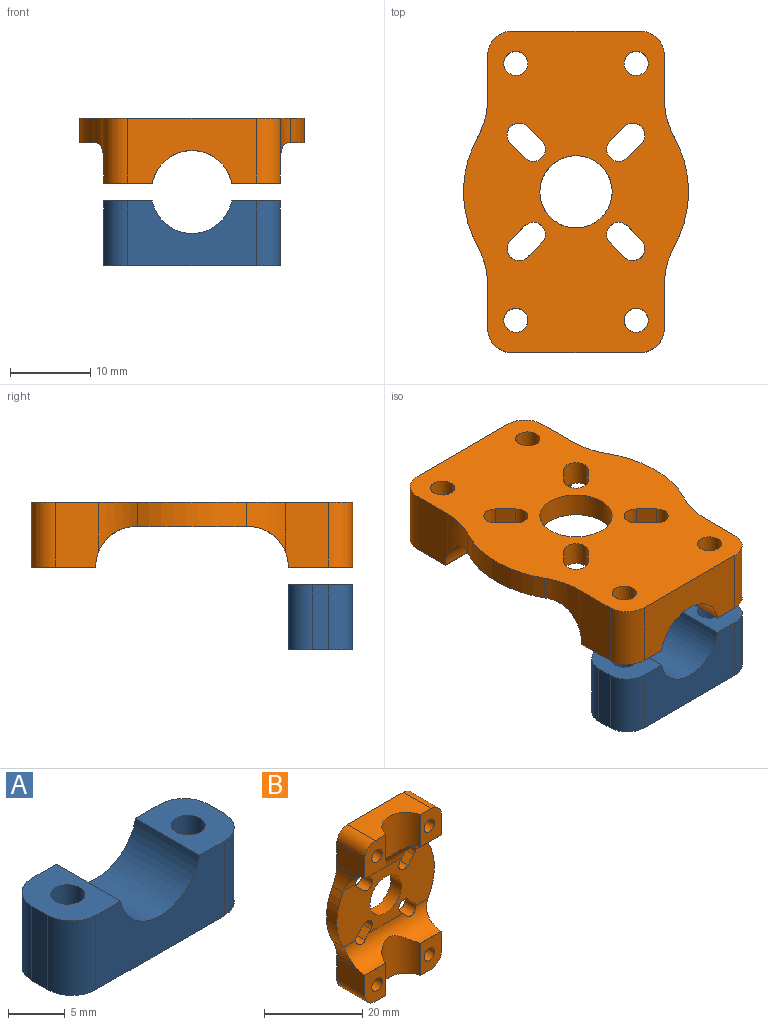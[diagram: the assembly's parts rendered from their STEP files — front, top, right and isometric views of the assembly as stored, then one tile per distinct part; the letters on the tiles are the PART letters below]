
ASSEMBLY  parts=2 mates=2
PART A: 14 faces, bbox 22x8x8.1 mm
  f0: cylinder r=5.05mm len=9.9mm, axis (0,1,0), area 110.8mm2, adj f3,f4,f5,f9
  f1: plane 22x8mm, normal (0,0,-1), area 154.1mm2, adj f2,f4,f5,f6,f7,f8,f10,f11
  f2: plane 8.05x2mm, normal (1,0,0), area 16.1mm2, adj f1,f3,f7,f8
  f3: plane 8x6.05mm, normal (0,0,1), area 37.5mm2, adj f0,f2,f4,f5,f6,f7,f8
  f4: plane 16x8.05mm, normal (0,-1,0), area 98.8mm2, adj f0,f1,f3,f8,f9,f13
  f5: plane 16x8.05mm, normal (0,1,0), area 98.8mm2, adj f0,f1,f3,f7,f9,f12
  f6: cylinder r=1.5mm len=8.05mm, axis (0,0,1), area 75.9mm2, adj f1,f3
  f7: cylinder r=3mm len=8.05mm, axis (0,0,1), area 37.9mm2, adj f1,f2,f3,f5
  f8: cylinder r=3mm len=8.05mm, axis (0,0,-1), area 37.9mm2, adj f1,f2,f3,f4
  f9: plane 8x6.05mm, normal (0,0,1), area 37.5mm2, adj f0,f4,f5,f10,f11,f12,f13
  f10: plane 8.05x2mm, normal (-1,0,0), area 16.1mm2, adj f1,f9,f12,f13
  f11: cylinder r=1.5mm len=8.05mm, axis (0,0,1), area 75.9mm2, adj f1,f9
  f12: cylinder r=3mm len=8.05mm, axis (0,0,-1), area 37.9mm2, adj f1,f5,f9,f10
  f13: cylinder r=3mm len=8.05mm, axis (0,0,1), area 37.9mm2, adj f1,f4,f9,f10
PART B: 51 faces, bbox 28x8.1x40 mm
  f0: plane 6.06x0.05mm, normal (0,0,-1), area 0.3mm2, adj f27,f28,f36,f46
  f1: plane 6.06x0.05mm, normal (0,0,1), area 0.3mm2, adj f29,f30,f31,f45
  f2: plane 16x8.05mm, normal (0,0,1), area 98.8mm2, adj f4,f5,f27,f28,f41,f42
  f3: plane 28x14mm, normal (0,-1,0), area 269.2mm2, adj f10,f11,f12,f13,f14,f15,f16,f17
  f4: plane 40x28mm, normal (0,1,0), area 795.9mm2, adj f2,f9,f10,f11,f12,f13,f14,f15
  f5: plane 8x6.05mm, normal (0,-1,0), area 39.4mm2, adj f2,f6,f28,f35,f39,f42
  f6: plane 6.06x0.05mm, normal (0,0,-1), area 0.3mm2, adj f5,f28,f35,f46
  f7: plane 8x6.05mm, normal (0,-1,0), area 39.4mm2, adj f8,f9,f30,f34,f38,f43
  f8: plane 6.06x0.05mm, normal (0,0,1), area 0.3mm2, adj f7,f30,f34,f45
  f9: plane 16x8.05mm, normal (0,0,-1), area 98.8mm2, adj f4,f7,f29,f30,f43,f44
  f10: cylinder r=1.5mm len=3mm, axis (0,-1,0), area 14.1mm2, adj f3,f4,f11,f25
  f11: plane 3x1.77mm, normal (0.71,0,0.71), area 7.5mm2, adj f3,f4,f10,f12
  f12: cylinder r=1.5mm len=3.25mm, axis (0,-1,0), area 14.7mm2, adj f3,f4,f11,f25,f46
  f13: plane 3x1.77mm, normal (0.71,0,-0.71), area 7.5mm2, adj f3,f4,f14,f22
  f14: cylinder r=1.5mm len=3mm, axis (0,-1,0), area 14.1mm2, adj f3,f4,f13,f15
  f15: plane 3.14x1.78mm, normal (-0.71,0,0.71), area 7.6mm2, adj f3,f4,f14,f22,f45
  f16: plane 3.14x1.78mm, normal (0.71,0,0.71), area 7.6mm2, adj f3,f4,f17,f23,f45
  f17: cylinder r=1.5mm len=3mm, axis (0,-1,0), area 14.1mm2, adj f3,f4,f16,f18
  f18: plane 3x1.77mm, normal (-0.71,0,-0.71), area 7.5mm2, adj f3,f4,f17,f23
  f19: plane 3x1.77mm, normal (-0.71,0,0.71), area 7.5mm2, adj f3,f4,f20,f24
  f20: cylinder r=1.5mm len=3mm, axis (0,-1,0), area 14.1mm2, adj f3,f4,f19,f21
  f21: plane 3.14x1.78mm, normal (0.71,0,-0.71), area 7.6mm2, adj f3,f4,f20,f24,f46
  f22: cylinder r=1.5mm len=3.25mm, axis (0,-1,0), area 14.7mm2, adj f3,f4,f13,f15,f45
  f23: cylinder r=1.5mm len=3.25mm, axis (0,-1,0), area 14.7mm2, adj f3,f4,f16,f18,f45
  f24: cylinder r=1.5mm len=3.25mm, axis (0,-1,0), area 14.7mm2, adj f3,f4,f19,f21,f46
  f25: plane 3.14x1.78mm, normal (-0.71,0,-0.71), area 7.6mm2, adj f3,f4,f10,f12,f46
  f26: cylinder r=4.5mm len=9mm, axis (0,1,0), area 84.8mm2, adj f3,f4
  f27: plane 8x6.05mm, normal (0,-1,0), area 39.4mm2, adj f0,f2,f28,f36,f40,f41
  f28: cylinder r=5.05mm len=10mm, axis (0,0,1), area 123.9mm2, adj f0,f2,f5,f6,f27,f46
  f29: plane 8x6.05mm, normal (0,-1,0), area 39.4mm2, adj f1,f9,f30,f31,f37,f44
  f30: cylinder r=5.05mm len=10mm, axis (0,0,-1), area 123.9mm2, adj f1,f7,f8,f9,f29,f45
  f31: plane 8.05x5.38mm, normal (1,0,0), area 42.8mm2, adj f1,f4,f29,f44,f45,f50
  f32: cylinder r=14mm len=13.56mm, axis (0,1,0), area 42.5mm2, adj f3,f4,f48,f50
  f33: cylinder r=14mm len=13.56mm, axis (0,1,0), area 42.5mm2, adj f3,f4,f47,f49
  f34: plane 8.05x5.38mm, normal (-1,0,0), area 42.8mm2, adj f4,f7,f8,f43,f45,f49
  f35: plane 8.05x5.38mm, normal (1,0,0), area 42.8mm2, adj f4,f5,f6,f42,f46,f48
  f36: plane 8.05x5.38mm, normal (-1,0,0), area 42.8mm2, adj f0,f4,f27,f41,f46,f47
  f37: cylinder r=1.5mm len=8.05mm, axis (0,1,0), area 75.9mm2, adj f4,f29
  f38: cylinder r=1.5mm len=8.05mm, axis (0,1,0), area 75.9mm2, adj f4,f7
  f39: cylinder r=1.5mm len=8.05mm, axis (0,1,0), area 75.9mm2, adj f4,f5
  f40: cylinder r=1.5mm len=8.05mm, axis (0,1,0), area 75.9mm2, adj f4,f27
  f41: cylinder r=3mm len=8.05mm, axis (0,1,0), area 37.9mm2, adj f2,f4,f27,f36
  f42: cylinder r=3mm len=8.05mm, axis (0,-1,0), area 37.9mm2, adj f2,f4,f5,f35
  f43: cylinder r=3mm len=8.05mm, axis (0,-1,0), area 37.9mm2, adj f4,f7,f9,f34
  f44: cylinder r=3mm len=8.05mm, axis (0,1,0), area 37.9mm2, adj f4,f9,f29,f31
  f45: cylinder r=5mm len=24.26mm, axis (1,0,0), area 135.5mm2, adj f1,f3,f8,f15,f16,f22,f23,f30
  f46: cylinder r=5mm len=24.26mm, axis (1,0,0), area 135.5mm2, adj f0,f3,f6,f12,f21,f24,f25,f28
  f47: cylinder r=10mm len=6.09mm, axis (0,1,0), area 19.2mm2, adj f3,f4,f33,f36,f46
  f48: cylinder r=10mm len=6.09mm, axis (0,1,0), area 19.2mm2, adj f3,f4,f32,f35,f46
  f49: cylinder r=10mm len=6.09mm, axis (0,1,0), area 19.2mm2, adj f3,f4,f33,f34,f45
  f50: cylinder r=10mm len=6.09mm, axis (0,1,0), area 19.2mm2, adj f3,f4,f31,f32,f45
PLACE A t=(-5.05,0.94,-18.81)mm
PLACE B rot(axis=(1,0,0),90deg) t=(-5.05,12.94,-3.49)mm
MATE planar B.f2 <-> A.f4  axis (0,-1,0) through (-5.05,-7.06,-3.81)mm
MATE cylindrical A.f11 <-> B.f40  axis (0,0,1) through (-12.55,-3.06,-14.79)mm
